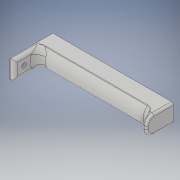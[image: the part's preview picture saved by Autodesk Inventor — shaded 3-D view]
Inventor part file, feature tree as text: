
AUTODESK INVENTOR PART (.ipt)
format: ipt  version: 2018 (Build 220112000, 112)  size: 346,624 bytes
history: native  units: in
note: dims shown in document units (in); Inventor stores cm internally (conversion verified against a paired STEP export)
features: extrude x7, sketch x7, projected_geometry x7, fillet x5, chamfer x1
ambient origin geometry x8: Origin, YZ Plane, XZ Plane, XY Plane, X Axis, Y Axis, Z Axis, Center Point
bodies: Solid1 (feature_tree)
feature tree (27):
  extrude  "Extrusion1"  Depth=0.5512in
  extrude  "Extrusion2"  Depth=1.5748in TaperAngle=0.0deg
  fillet  "Fillet3"  Radius=1.5748in
  fillet  "Fillet4"  Radius=0.1575in
  extrude  "Extrusion3"  Depth=0.1181in
  extrude  "Extrusion4"  Depth=0.1181in TaperAngle=0.0deg
  fillet  "Fillet5"  Radius=0.9843in
  fillet  "Fillet6"  Radius=0.1181in
  fillet  "Fillet7"  Radius=0.2756in
  extrude  "Extrusion5"  Depth=0.0394in
  chamfer  "Chamfer1"  Distance=0.1181in
  extrude  "Extrusion6"  Depth=0.1181in TaperAngle=45.0deg
  extrude  "Extrusion7"  Depth=0.1181in
  sketch  "Sketch1"  dims[d1=0.6693in d2=0.5512in]
  sketch  "Sketch2"  dims[d3=0.4331in d4=4.1339in d5=0.0in d6=1.5748in d7=0.1575in d8=0.0in]
  sketch  "Sketch3"  dims[d11=0.1181in d12=0.2756in]
  sketch  "Sketch4"  dims[d13=0.1654in d14=0.1575in d15=0.0in d16=0.9843in d17=0.1181in d18=0.0in d19=0.2756in]
  sketch  "Sketch5"  dims[d20=0.0787in d21=0.0394in]
  sketch  "Sketch6"  dims[d22=0.1969in]
  projected_geometry  "Projected Loop1"
  projected_geometry  "Projected Loop2"
  projected_geometry  "Projected Loop3"
  projected_geometry  "Projected Loop4"
  projected_geometry  "Projected Loop5"
  projected_geometry  "Projected Loop6"
  sketch  "Sketch7"  dims[d23=0.3937in d24=0.1181in d25=0.0in d26=0.0787in d27=0.0787in d28=45.0deg d29=0.1969in d31=0.5512in d32=0.4331in d33=4.1339in d34=0.0in d35=0.1181in d36=0.0in]
  projected_geometry  "Projected Loop7"
